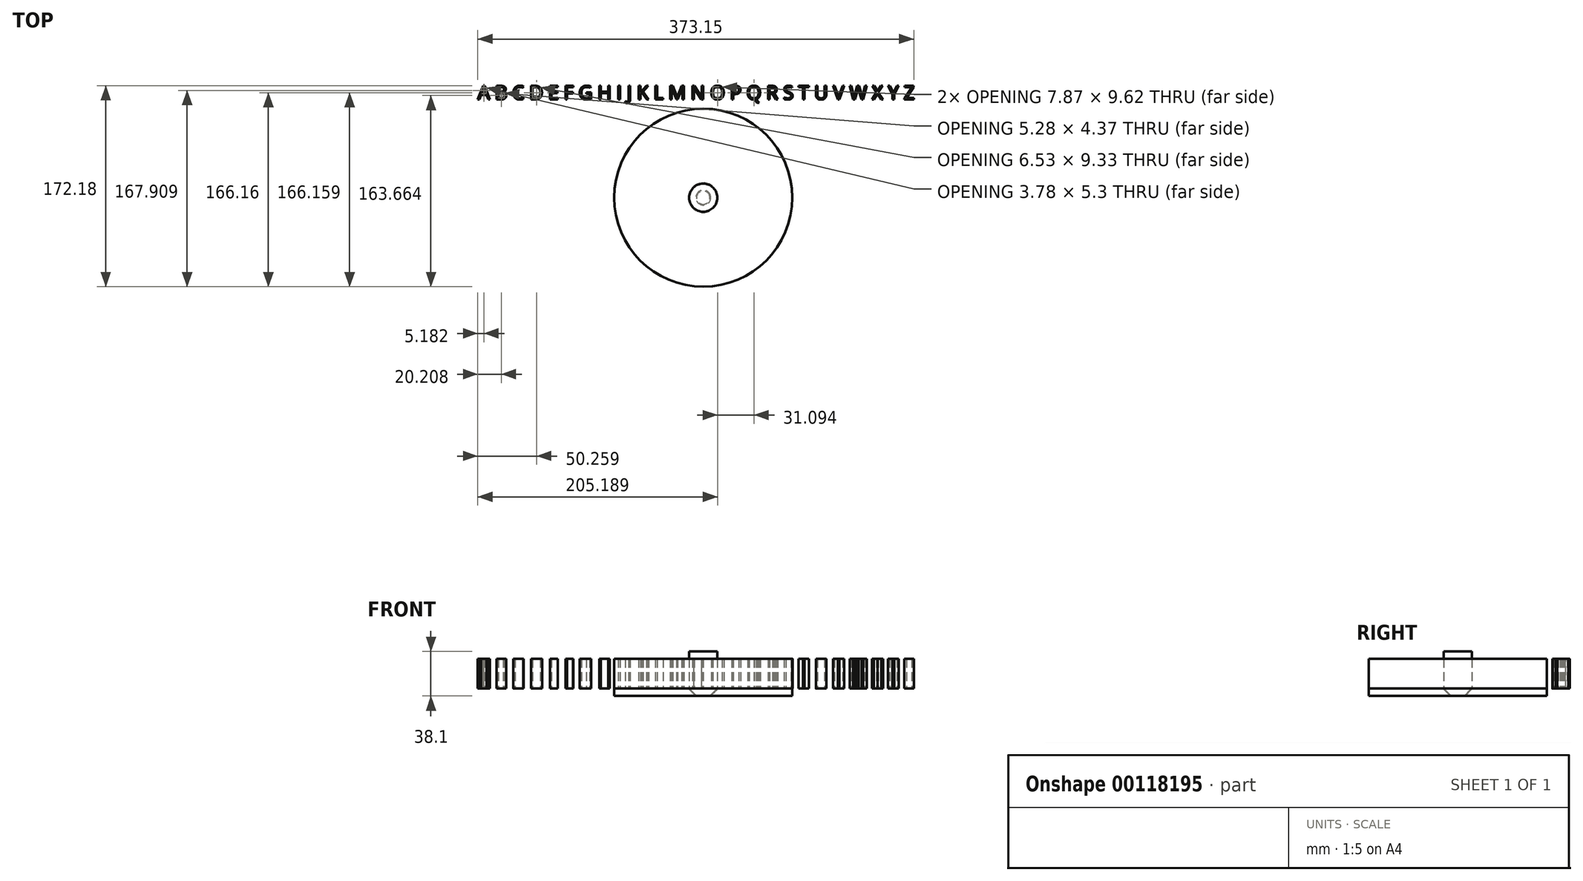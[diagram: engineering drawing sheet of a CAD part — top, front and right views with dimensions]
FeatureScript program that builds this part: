
annotation { "Feature Type Name" : "Feature", "Feature Type Description" : "" }
export const myFeature = defineFeature(function(context is Context, id is Id, definition is map)
    precondition{}
    {
        {
            var Q0;
            Q0=qCreatedBy(makeId("Top.planeOp"),FACE);
            var sketch = newSketch(context, id + "F0", { "sketchPlane" : qUnion([Q0])});
            skCircle(sketch, "E0", {"center": v(0, 0) * mm, "radius": 12.06 * mm});
            skSolve(sketch);
        }
        {
            var Q0;
            Q0 = qSketchRegion(id + "F0", true);
            extrude(context, id + "F1", {"entities" : qUnion([Q0]), "depth" : 31.75 * mm, "hasSecondDirection" : true, "secondDirectionOppositeDirection" : true, "secondDirectionDepth" : 6.35 * mm});
        }
        {
            var Q0;
            Q0=makeQuery(id+"F1.opExtrude","CAP_FACE",FACE,{"disambiguationData":[OSD([sQuery(id+"F0.wireOp",EDGE,"E0")])],"isStart":true});
            var sketch = newSketch(context, id + "F2", { "sketchPlane" : qUnion([Q0])});
            skCircle(sketch, "E1", {"center": v(0, 0) * mm, "radius": 76.2 * mm});
            skSolve(sketch);
        }
        {
            var Q0;
            Q0 = qSketchRegion(id + "F2", true);
            extrude(context, id + "F3", {"entities" : qUnion([Q0]), "oppositeDirection" : true, "depth" : 6.35 * mm});
        }
        {
            var Q0;
            Q0=sQuery(id+"F0.wireOp",VERTEX,"E0.center");
            var Q1;
            Q1=makeQuery(id+"F3.opExtrude","SWEPT_BODY",BODY,{"disambiguationData":[OSD([sQuery(id+"F2.wireOp",EDGE,"E1")])]});
            hole(context, id + "F4", {"style" : HoleStyle.C_SINK, "endStyle" : HoleEndStyle.THROUGH, "holeDiameter" : 12.7 * mm, "cSinkDiameter" : 25.4 * mm, "cSinkAngle" : 90 * degree, "locations" : qUnion([Q0]), "scope" : qUnion([Q1]), "isTappedThrough" : true});
        }
        {
            var Q0;
            Q0=makeQuery(id+"F1.opExtrude","CAP_EDGE",EDGE,{"disambiguationData":[OSD([sQuery(id+"F0.wireOp",EDGE,"E0")])],"isStart":true});
            chamfer(context, id + "F5", {"entities" : qUnion([Q0]), "chamferType" : ChamferType.TWO_OFFSETS, "width1" : 6.35 * mm, "oppositeDirection" : false, "width2" : 6.35 * mm, "tangentPropagation" : true});
        }
        {
            var Q0;
            Q0=qCreatedBy(makeId("Top.planeOp"),FACE);
            var sketch = newSketch(context, id + "F6", { "sketchPlane" : qUnion([Q0])});
            skCircle(sketch, "E2", {"center": v(0, 0) * mm, "radius": 76.2 * mm});
            skText(sketch, "E3", { "text": "A B C D E F G H I J K L M N O P Q R S T U V W X Y Z", "fontName": "OpenSans-Regular.ttf"});
            const initialGuessF6  = {"E3": [-0.19294, 0.08412, 1, 0, 0.01178]};
            skSetInitialGuess(sketch, initialGuessF6);
            skSolve(sketch);
        }
        {
            var Q0;
            Q0 = qSketchRegion(id + "F6", true);
            extrude(context, id + "F7", {"entities" : qUnion([Q0]), "depth" : 25.4 * mm});
        }
    });
